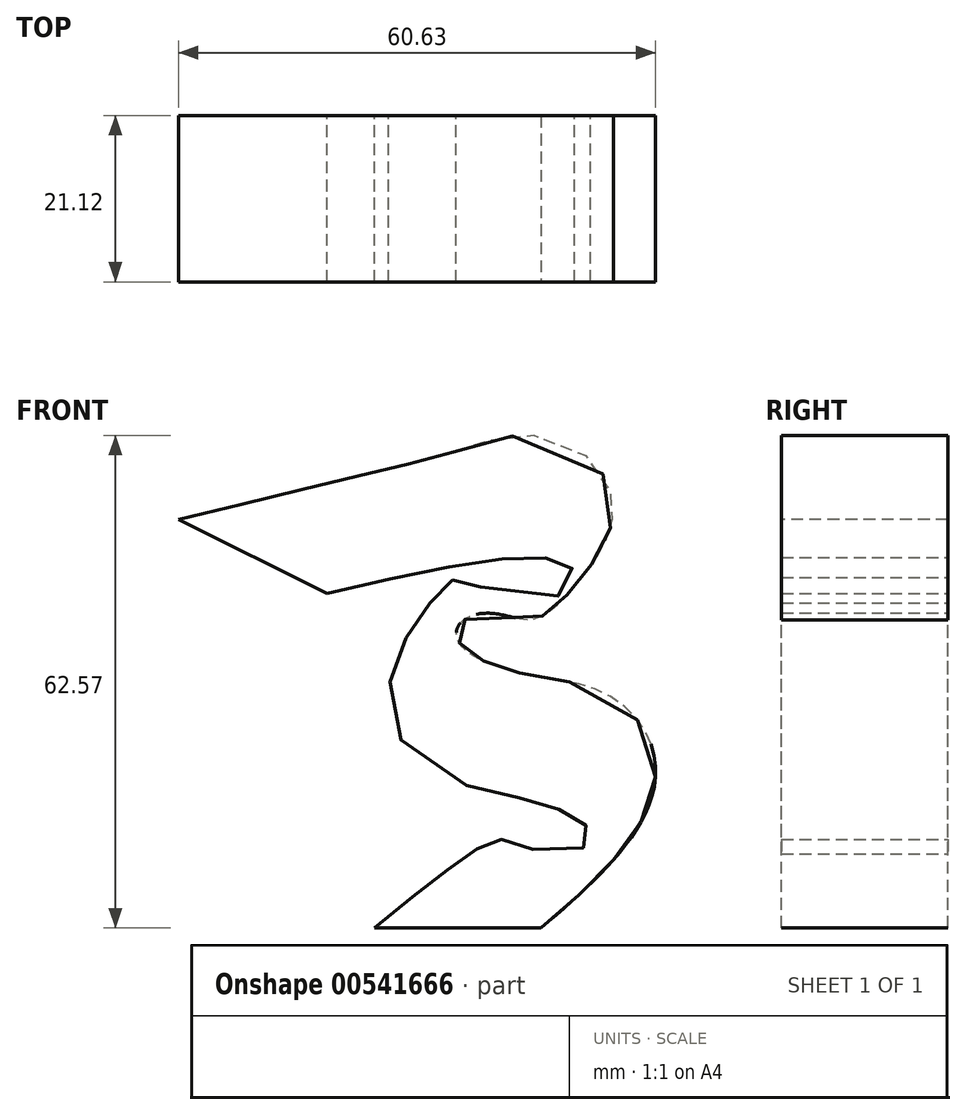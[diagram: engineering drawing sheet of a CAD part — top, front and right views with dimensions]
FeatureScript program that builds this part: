
annotation { "Feature Type Name" : "Feature", "Feature Type Description" : "" }
export const myFeature = defineFeature(function(context is Context, id is Id, definition is map)
    precondition{}
    {
        {
            var Q0;
            Q0=qCreatedBy(makeId("Top.planeOp"),FACE);
            var sketch = newSketch(context, id + "F0", { "sketchPlane" : qUnion([Q0])});
            skLineSegment(sketch, "E0", {"start": v(-10.56, 10.56) * mm, "end": v(10.56, 10.56) * mm});
            skLineSegment(sketch, "E1", {"start": v(10.56, 10.56) * mm, "end": v(10.56, -10.56) * mm});
            skLineSegment(sketch, "E2", {"start": v(10.56, -10.56) * mm, "end": v(-10.56, -10.56) * mm});
            skLineSegment(sketch, "E3", {"start": v(-10.56, -10.56) * mm, "end": v(-10.56, 10.56) * mm});
            skPoint(sketch, "E4", {"position": v(0, 10.56) * mm});
            skPoint(sketch, "E5", {"position": v(10.56, 0) * mm});
            skSolve(sketch);
        }
        {
            var Q0;
            Q0=qCreatedBy(makeId("Front.planeOp"),FACE);
            var sketch = newSketch(context, id + "F1", { "sketchPlane" : qUnion([Q0])});
            skFitSpline(sketch, "E6", {"points": [v(0, 0) * mm, v(15.58, 20.1) * mm, v(0, 30.54) * mm, v(10.67, 50.68) * mm, v(-26.04, 47.17) * mm], "startDerivative": vector(112.26, 93.92) * mm, "endDerivative": vector(-184.5, -44.24) * mm});
            skSolve(sketch);
        }
        {
            var Q0;
            Q0=makeQuery(id+"F0.imprint","IMPRINT",FACE,{"disambiguationData":[TD([[makeQuery(id+"F0.imprint","IMPRINT",EDGE,{"derivedFrom":sQuery(id+"F0.wireOp",EDGE,"E0")}),-1.0]])]});
            var Q1;
            Q1=sQuery(id+"F1.wireOp",EDGE,"E6");
            sweep(context, id + "F2", {"profiles" : qUnion([Q0]), "path" : qUnion([Q1])});
        }
    });
